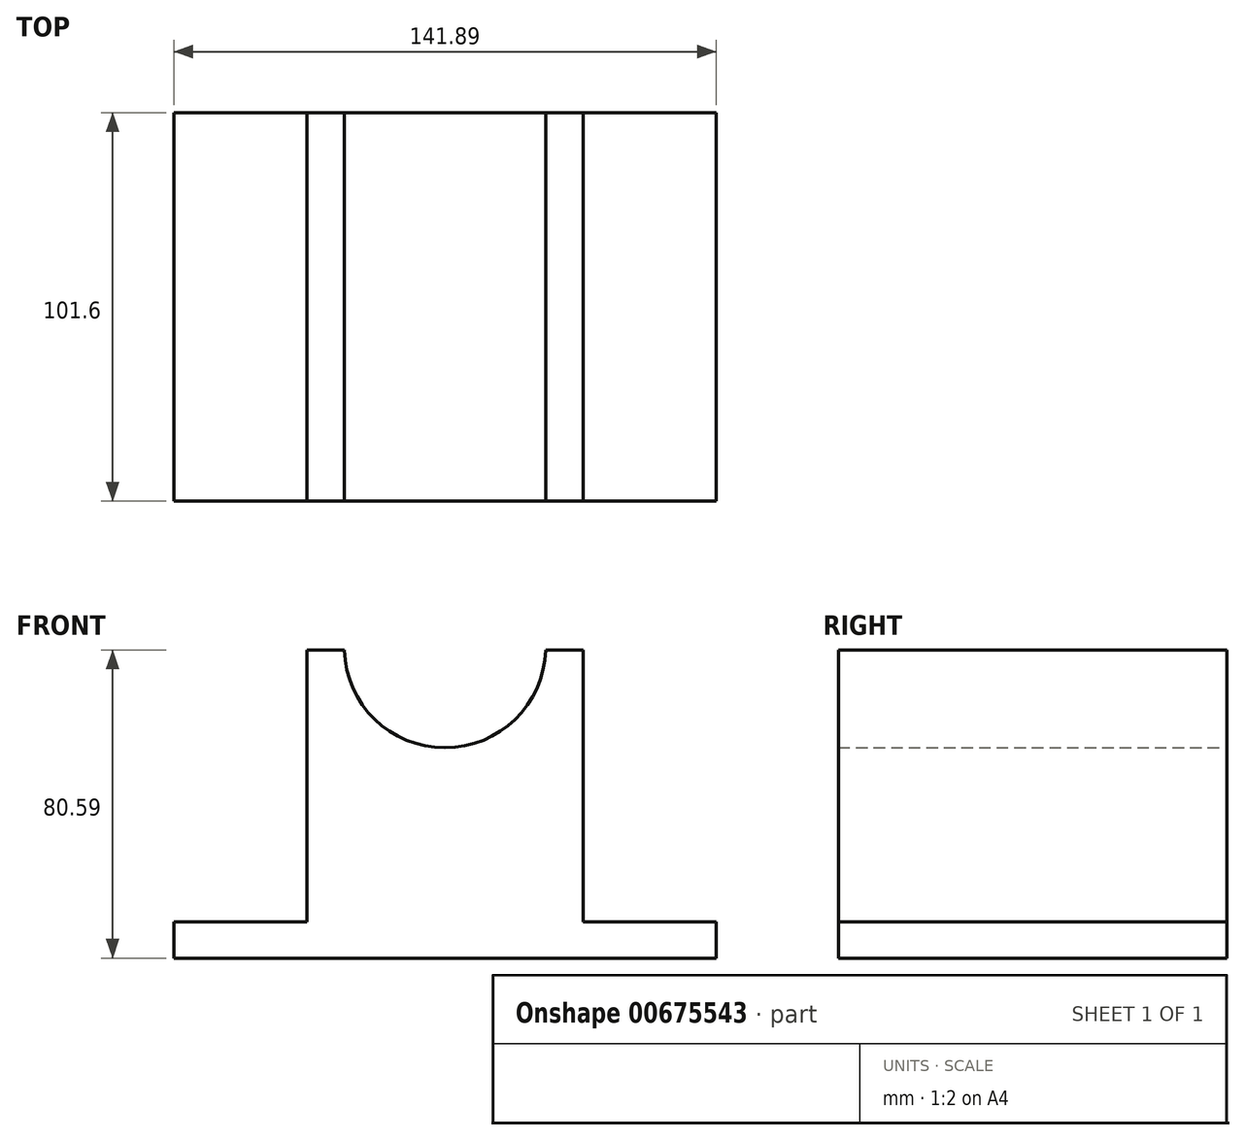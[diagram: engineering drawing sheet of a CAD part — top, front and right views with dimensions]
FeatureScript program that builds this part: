
annotation { "Feature Type Name" : "Feature", "Feature Type Description" : "" }
export const myFeature = defineFeature(function(context is Context, id is Id, definition is map)
    precondition{}
    {
        {
            var Q0;
            Q0=qCreatedBy(makeId("Front.planeOp"),FACE);
            var sketch = newSketch(context, id + "F0", { "sketchPlane" : qUnion([Q0])});
            skLineSegment(sketch, "E0", {"start": v(-33.24, 50.5) * mm, "end": v(-33.24, -20.58) * mm});
            skLineSegment(sketch, "E1", {"start": v(-33.24, -20.58) * mm, "end": v(-68.07, -20.58) * mm});
            skLineSegment(sketch, "E2", {"start": v(-68.07, -20.58) * mm, "end": v(-68.07, -30.08) * mm});
            skLineSegment(sketch, "E3", {"start": v(-68.07, -30.08) * mm, "end": v(73.82, -30.08) * mm});
            skLineSegment(sketch, "E4", {"start": v(73.82, -30.08) * mm, "end": v(73.82, -20.58) * mm});
            skLineSegment(sketch, "E5", {"start": v(73.82, -20.58) * mm, "end": v(39, -20.58) * mm});
            skLineSegment(sketch, "E6", {"start": v(39, -20.58) * mm, "end": v(39, 50.5) * mm});
            skLineSegment(sketch, "E7", {"start": v(39, 50.5) * mm, "end": v(29.21, 50.5) * mm});
            skLineSegment(sketch, "E8", {"start": v(-33.24, 50.5) * mm, "end": v(-23.46, 50.5) * mm});
            skArc(sketch, "E9", {"start": v(-23.46, 50.5) * mm, "mid": v(2.88, 24.93) * mm, "end": v(29.21, 50.5) * mm});
            skSolve(sketch);
        }
        {
            var Q0;
            Q0 = qSketchRegion(id + "F0", true);
            extrude(context, id + "F1", {"entities" : qUnion([Q0]), "depth" : 101.6 * mm, "offsetDistance" : 25.4 * mm});
        }
    });
